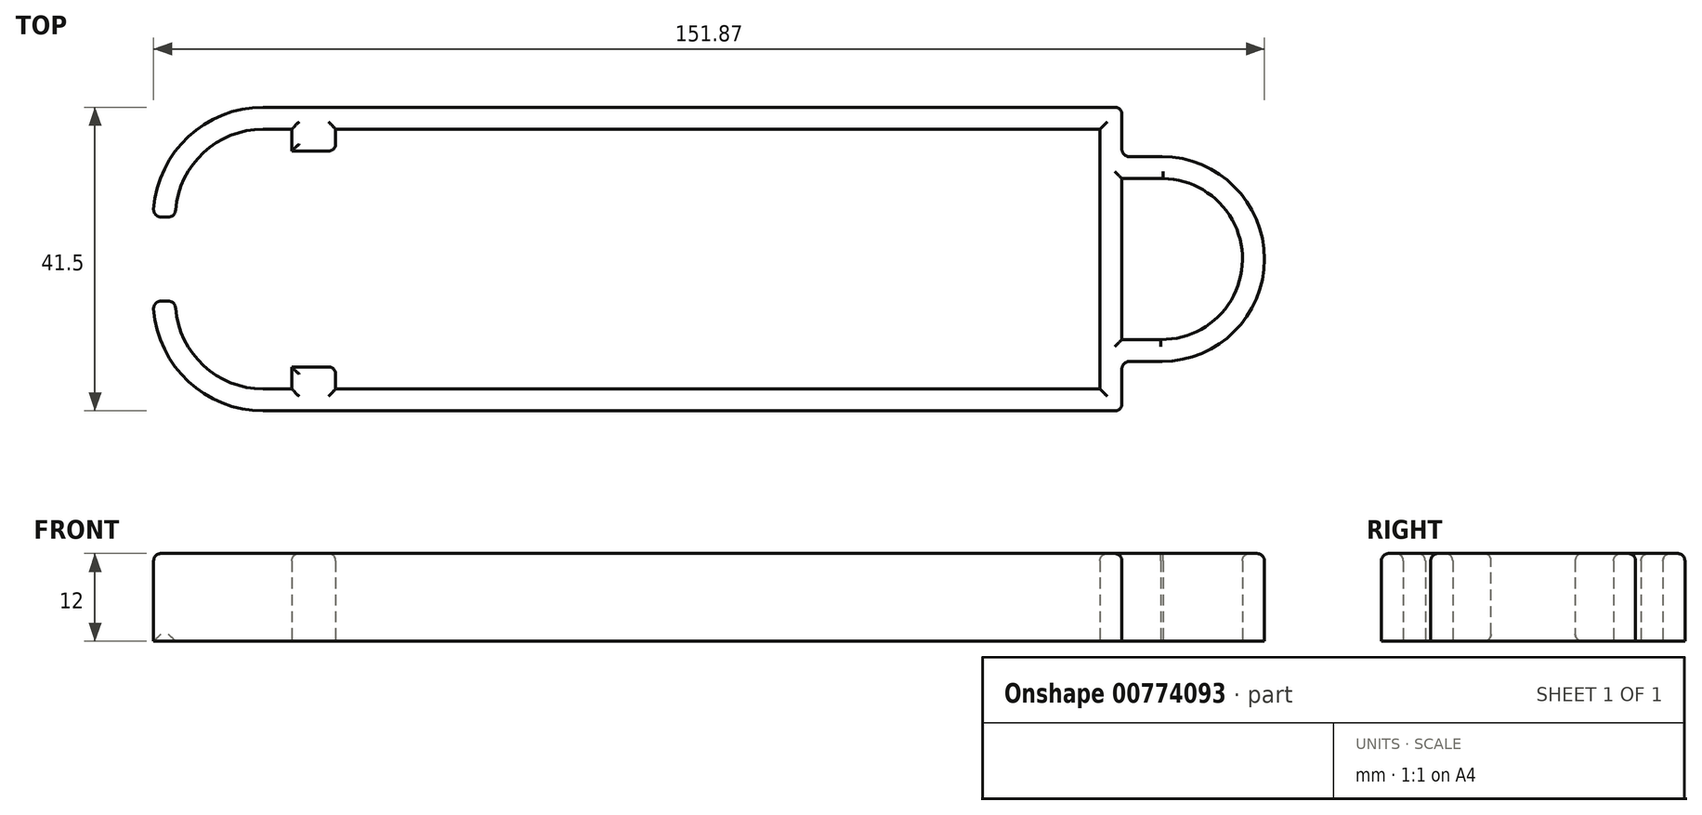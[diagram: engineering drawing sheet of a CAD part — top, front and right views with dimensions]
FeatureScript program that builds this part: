
annotation { "Feature Type Name" : "Feature", "Feature Type Description" : "" }
export const myFeature = defineFeature(function(context is Context, id is Id, definition is map)
    precondition{}
    {
        {
            var Q0;
            Q0=qCreatedBy(makeId("Top.planeOp"),FACE);
            var sketch = newSketch(context, id + "F0", { "sketchPlane" : qUnion([Q0])});
            skLineSegment(sketch, "E0.bottom", {"start": v(0, 0) * mm, "end": v(-104.5, 0) * mm, "construction": true});
            skLineSegment(sketch, "E0.top", {"start": v(0, -35.5) * mm, "end": v(-104.5, -35.5) * mm, "construction": true});
            skLineSegment(sketch, "E0.left", {"start": v(0, 0) * mm, "end": v(0, -35.5) * mm, "construction": true});
            skLineSegment(sketch, "E0.right", {"start": v(-104.5, 0) * mm, "end": v(-104.5, -3) * mm, "construction": true});
            skLineSegment(sketch, "E1.bottom", {"start": v(-104.5, -32.5) * mm, "end": v(-107.5, -32.5) * mm, "construction": true});
            skLineSegment(sketch, "E1.top", {"start": v(-104.5, -3) * mm, "end": v(-107.5, -3) * mm, "construction": true});
            skLineSegment(sketch, "E1.right", {"start": v(-107.5, -32.5) * mm, "end": v(-107.5, -19.25) * mm, "construction": true});
            skLineSegment(sketch, "E2.bottom", {"start": v(-107.5, -16.25) * mm, "end": v(-148.78, -16.25) * mm, "construction": true});
            skLineSegment(sketch, "E2.top", {"start": v(-107.5, -19.25) * mm, "end": v(-148.78, -19.25) * mm, "construction": true});
            skLineSegment(sketch, "E2.right", {"start": v(-148.78, -16.25) * mm, "end": v(-148.78, -19.25) * mm, "construction": true});
            skLineSegment(sketch, "E3.trimOffspring", {"start": v(-107.5, -16.25) * mm, "end": v(-107.5, -3) * mm, "construction": true});
            skLineSegment(sketch, "E4.trimOffspring", {"start": v(-104.5, -32.5) * mm, "end": v(-104.5, -35.5) * mm, "construction": true});
            skSolve(sketch);
        }
        {
            var Q0;
            Q0=qCreatedBy(makeId("Top.planeOp"),FACE);
            var sketch = newSketch(context, id + "F1", { "sketchPlane" : qUnion([Q0])});
            skLineSegment(sketch, "E5.bottom", {"start": v(0, 0) * mm, "end": v(-104.5, 0) * mm});
            skLineSegment(sketch, "E5.top", {"start": v(0, 3) * mm, "end": v(-114.42, 3) * mm});
            skLineSegment(sketch, "E5.left", {"start": v(0, 0) * mm, "end": v(0, 3) * mm});
            skLineSegment(sketch, "E6.bottom", {"start": v(0, -35.5) * mm, "end": v(-104.5, -35.5) * mm});
            skLineSegment(sketch, "E6.top", {"start": v(0, -38.5) * mm, "end": v(-114.42, -38.5) * mm});
            skLineSegment(sketch, "E6.left", {"start": v(0, -35.5) * mm, "end": v(0, -38.5) * mm});
            skLineSegment(sketch, "E7.top", {"start": v(-104.5, -3) * mm, "end": v(-110.5, -3) * mm});
            skLineSegment(sketch, "E7.left", {"start": v(-104.5, 0) * mm, "end": v(-104.5, -3) * mm});
            skLineSegment(sketch, "E7.right", {"start": v(-110.5, 0) * mm, "end": v(-110.5, -3) * mm});
            skLineSegment(sketch, "E8.top", {"start": v(-110.5, -32.5) * mm, "end": v(-104.5, -32.5) * mm});
            skLineSegment(sketch, "E8.left", {"start": v(-110.5, -35.5) * mm, "end": v(-110.5, -32.5) * mm});
            skLineSegment(sketch, "E8.right", {"start": v(-104.5, -35.5) * mm, "end": v(-104.5, -32.5) * mm});
            skArc(sketch, "E9", {"start": v(-114.42, 3) * mm, "mid": v(-125.03, -1.4) * mm, "end": v(-129.42, -12) * mm});
            skArc(sketch, "E10", {"start": v(-114.42, 0) * mm, "mid": v(-122.9, -3.51) * mm, "end": v(-126.42, -12) * mm});
            skLineSegment(sketch, "E11.bottom", {"start": v(-129.42, -12) * mm, "end": v(-126.42, -12) * mm});
            skArc(sketch, "E12", {"start": v(-129.42, -23.5) * mm, "mid": v(-125.03, -34.1) * mm, "end": v(-114.42, -38.5) * mm});
            skArc(sketch, "E13", {"start": v(-126.42, -23.5) * mm, "mid": v(-122.9, -31.99) * mm, "end": v(-114.42, -35.5) * mm});
            skLineSegment(sketch, "E14.bottom", {"start": v(-126.42, -23.5) * mm, "end": v(-129.42, -23.5) * mm});
            skLineSegment(sketch, "E15.trimOffspring", {"start": v(-110.5, -35.5) * mm, "end": v(-114.42, -35.5) * mm});
            skLineSegment(sketch, "E16.trimOffspring", {"start": v(-110.5, 0) * mm, "end": v(-114.42, 0) * mm});
            skLineSegment(sketch, "E17.bottom", {"start": v(0, -38.5) * mm, "end": v(3, -38.5) * mm});
            skLineSegment(sketch, "E17.top", {"start": v(0, 3) * mm, "end": v(3, 3) * mm});
            skLineSegment(sketch, "E17.left", {"start": v(0, -38.5) * mm, "end": v(0, 3) * mm});
            skLineSegment(sketch, "E17.right", {"start": v(3, -38.5) * mm, "end": v(3, -31.75) * mm});
            skArc(sketch, "E18", {"start": v(8.48, -31.75) * mm, "mid": v(22.48, -17.75) * mm, "end": v(8.48, -3.75) * mm});
            skArc(sketch, "E19", {"start": v(8.35, -28.75) * mm, "mid": v(19.48, -17.88) * mm, "end": v(8.61, -6.75) * mm});
            skLineSegment(sketch, "E20.bottom", {"start": v(8.48, -3.75) * mm, "end": v(3, -3.75) * mm});
            skLineSegment(sketch, "E20.top", {"start": v(8.48, -31.75) * mm, "end": v(3, -31.75) * mm});
            skLineSegment(sketch, "E21.bottom", {"start": v(3, -6.75) * mm, "end": v(8.61, -6.75) * mm});
            skLineSegment(sketch, "E21.top", {"start": v(3, -28.75) * mm, "end": v(8.35, -28.75) * mm});
            skPoint(sketch, "E22.orphan", {"position": v(63.3, -6.49) * mm});
            skPoint(sketch, "E23.trimOffspring.end.orphan", {"position": v(63.3, -28.49) * mm});
            skLineSegment(sketch, "E24.trimOffspring", {"start": v(3, -28.75) * mm, "end": v(3, -6.75) * mm});
            skLineSegment(sketch, "E25.trimOffspring", {"start": v(3, -3.75) * mm, "end": v(3, 3) * mm});
            skSolve(sketch);
        }
        {
            var Q0;
            Q0 = qSketchRegion(id + "F1", true);
            extrude(context, id + "F2", {"entities" : qUnion([Q0]), "depth" : 12 * mm, "offsetDistance" : 25 * mm});
        }
        {
            var Q0;
            Q0=makeQuery(id+"F2.opExtrude","SWEPT_EDGE",EDGE,{"disambiguationData":[OSD([sQuery(id+"F1.wireOp",EDGE,"E17.bottom"),sQuery(id+"F1.wireOp",EDGE,"E17.right")])]});
            var Q1;
            Q1=makeQuery(id+"F2.opExtrude","SWEPT_EDGE",EDGE,{"disambiguationData":[OSD([sQuery(id+"F1.wireOp",EDGE,"E17.right"),sQuery(id+"F1.wireOp",EDGE,"E20.top")])]});
            var Q2;
            Q2=makeQuery(id+"F2.opExtrude","SWEPT_EDGE",EDGE,{"disambiguationData":[OSD([sQuery(id+"F1.wireOp",EDGE,"E17.top"),sQuery(id+"F1.wireOp",EDGE,"E25.trimOffspring")])]});
            var Q3;
            Q3=makeQuery(id+"F2.opExtrude","CAP_FACE",FACE,{"disambiguationData":[OSD([sQuery(id+"F1.wireOp",EDGE,"E5.bottom"),sQuery(id+"F1.wireOp",EDGE,"E5.top"),sQuery(id+"F1.wireOp",EDGE,"E6.bottom"),sQuery(id+"F1.wireOp",EDGE,"E6.top"),sQuery(id+"F1.wireOp",EDGE,"E7.top"),sQuery(id+"F1.wireOp",EDGE,"E7.left"),sQuery(id+"F1.wireOp",EDGE,"E7.right"),sQuery(id+"F1.wireOp",EDGE,"E8.top"),sQuery(id+"F1.wireOp",EDGE,"E8.left"),sQuery(id+"F1.wireOp",EDGE,"E8.right"),sQuery(id+"F1.wireOp",EDGE,"E9"),sQuery(id+"F1.wireOp",EDGE,"E10"),sQuery(id+"F1.wireOp",EDGE,"E11.bottom"),sQuery(id+"F1.wireOp",EDGE,"E12"),sQuery(id+"F1.wireOp",EDGE,"E13"),sQuery(id+"F1.wireOp",EDGE,"E14.bottom"),sQuery(id+"F1.wireOp",EDGE,"E15.trimOffspring"),sQuery(id+"F1.wireOp",EDGE,"E16.trimOffspring"),sQuery(id+"F1.wireOp",EDGE,"E17.bottom"),sQuery(id+"F1.wireOp",EDGE,"E17.top"),sQuery(id+"F1.wireOp",EDGE,"E17.left"),sQuery(id+"F1.wireOp",EDGE,"E17.right"),sQuery(id+"F1.wireOp",EDGE,"E18"),sQuery(id+"F1.wireOp",EDGE,"E19"),sQuery(id+"F1.wireOp",EDGE,"E20.bottom"),sQuery(id+"F1.wireOp",EDGE,"E20.top"),sQuery(id+"F1.wireOp",EDGE,"E21.bottom"),sQuery(id+"F1.wireOp",EDGE,"E21.top"),sQuery(id+"F1.wireOp",EDGE,"E24.trimOffspring"),sQuery(id+"F1.wireOp",EDGE,"E25.trimOffspring")])],"isStart":false});
            var Q4;
            Q4=makeQuery(id+"F2.opExtrude","SWEPT_EDGE",EDGE,{"disambiguationData":[OSD([sQuery(id+"F1.wireOp",EDGE,"E20.bottom"),sQuery(id+"F1.wireOp",EDGE,"E25.trimOffspring")])]});
            var Q5;
            Q5=makeQuery(id+"F2.opExtrude","SWEPT_FACE",FACE,{"disambiguationData":[OSD([sQuery(id+"F1.wireOp",EDGE,"E11.bottom")])]});
            var Q6;
            Q6=makeQuery(id+"F2.opExtrude","SWEPT_FACE",FACE,{"disambiguationData":[OSD([sQuery(id+"F1.wireOp",EDGE,"E14.bottom")])]});
            var Q7;
            Q7=makeQuery(id+"F2.opExtrude","SWEPT_EDGE",EDGE,{"disambiguationData":[OSD([sQuery(id+"F1.wireOp",EDGE,"E8.top"),sQuery(id+"F1.wireOp",EDGE,"E8.right")])]});
            var Q8;
            Q8=makeQuery(id+"F2.opExtrude","SWEPT_EDGE",EDGE,{"disambiguationData":[OSD([sQuery(id+"F1.wireOp",EDGE,"E7.top"),sQuery(id+"F1.wireOp",EDGE,"E7.left")])]});
            fillet(context, id + "F3", {"entities" : qUnion([Q0, Q1, Q2, Q3, Q4, Q5, Q6, Q7, Q8]), "radius" : 1 * mm, "tangentPropagation" : true, "allowEdgeOverflow" : false});
        }
    });
